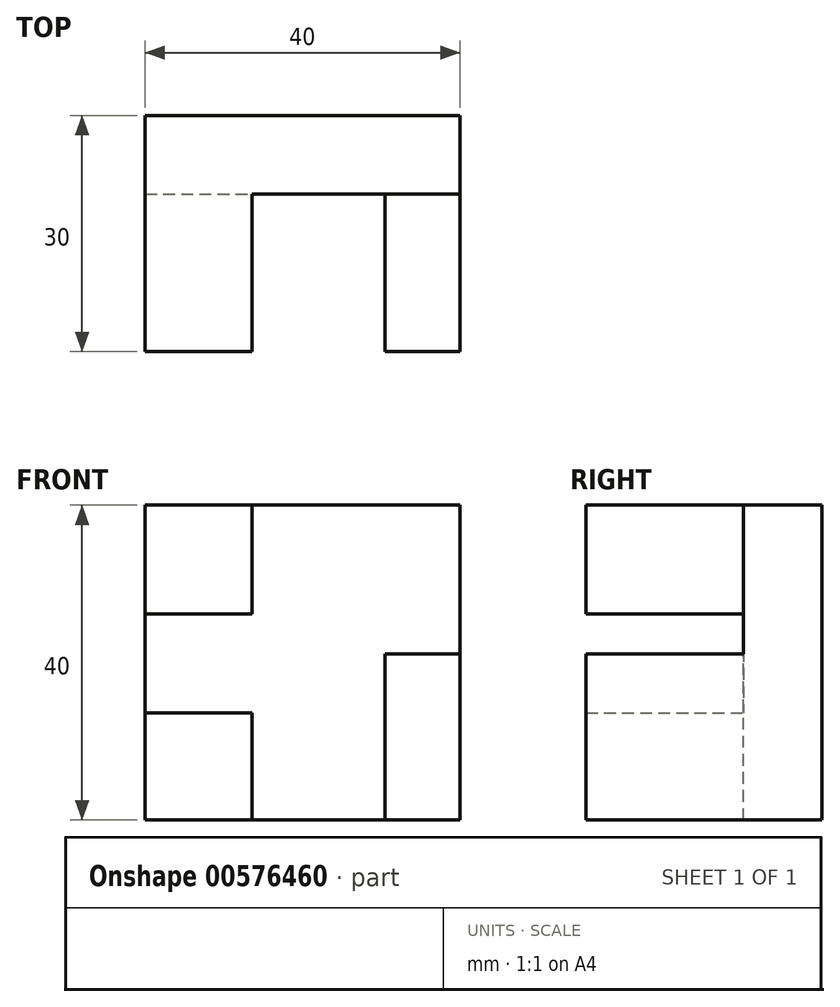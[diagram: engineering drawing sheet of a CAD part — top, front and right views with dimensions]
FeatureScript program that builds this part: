
annotation { "Feature Type Name" : "Feature", "Feature Type Description" : "" }
export const myFeature = defineFeature(function(context is Context, id is Id, definition is map)
    precondition{}
    {
        {
            var Q0;
            Q0=qCreatedBy(makeId("Front.planeOp"),FACE);
            var sketch = newSketch(context, id + "F0", { "sketchPlane" : qUnion([Q0])});
            skLineSegment(sketch, "E0.bottom", {"start": v(-28.84, 42.03) * mm, "end": v(11.16, 42.03) * mm});
            skLineSegment(sketch, "E0.top", {"start": v(-28.84, 2.03) * mm, "end": v(11.16, 2.03) * mm});
            skLineSegment(sketch, "E0.left", {"start": v(-28.84, 42.03) * mm, "end": v(-28.84, 2.03) * mm});
            skLineSegment(sketch, "E0.right", {"start": v(11.16, 42.03) * mm, "end": v(11.16, 2.03) * mm});
            skSolve(sketch);
        }
        {
            var Q0;
            Q0=makeQuery(id+"F0.imprint","IMPRINT",FACE,{"disambiguationData":[TD([[makeQuery(id+"F0.imprint","IMPRINT",EDGE,{"derivedFrom":sQuery(id+"F0.wireOp",EDGE,"E0.bottom")}),-1.0]])]});
            extrude(context, id + "F1", {"entities" : qUnion([Q0]), "depth" : 10 * mm, "offsetDistance" : 25 * mm});
        }
        {
            var Q0;
            Q0=makeQuery(id+"F1.opExtrude","CAP_FACE",FACE,{"disambiguationData":[OSD([sQuery(id+"F0.wireOp",EDGE,"E0.bottom"),sQuery(id+"F0.wireOp",EDGE,"E0.top"),sQuery(id+"F0.wireOp",EDGE,"E0.left"),sQuery(id+"F0.wireOp",EDGE,"E0.right")])],"isStart":false});
            var sketch = newSketch(context, id + "F2", { "sketchPlane" : qUnion([Q0])});
            skLineSegment(sketch, "E1.bottom", {"start": v(-28.84, 42.03) * mm, "end": v(-15.23, 42.03) * mm});
            skLineSegment(sketch, "E1.top", {"start": v(-28.84, 28.23) * mm, "end": v(-15.23, 28.23) * mm});
            skLineSegment(sketch, "E1.left", {"start": v(-28.84, 42.03) * mm, "end": v(-28.84, 28.23) * mm});
            skLineSegment(sketch, "E1.right", {"start": v(-15.23, 42.03) * mm, "end": v(-15.23, 28.23) * mm});
            skLineSegment(sketch, "E2.bottom", {"start": v(11.16, 2.03) * mm, "end": v(1.62, 2.03) * mm});
            skLineSegment(sketch, "E2.top", {"start": v(11.16, 23.15) * mm, "end": v(1.62, 23.15) * mm});
            skLineSegment(sketch, "E2.left", {"start": v(11.16, 2.03) * mm, "end": v(11.16, 23.15) * mm});
            skLineSegment(sketch, "E2.right", {"start": v(1.62, 2.03) * mm, "end": v(1.62, 23.15) * mm});
            skLineSegment(sketch, "E3.bottom", {"start": v(-15.23, 2.03) * mm, "end": v(-28.84, 2.03) * mm});
            skLineSegment(sketch, "E3.top", {"start": v(-15.23, 15.64) * mm, "end": v(-28.84, 15.64) * mm});
            skLineSegment(sketch, "E3.left", {"start": v(-15.23, 2.03) * mm, "end": v(-15.23, 15.64) * mm});
            skLineSegment(sketch, "E3.right", {"start": v(-28.84, 2.03) * mm, "end": v(-28.84, 15.64) * mm});
            skSolve(sketch);
        }
        {
            var Q0;
            Q0=makeQuery(id+"F2.imprint","IMPRINT",FACE,{"disambiguationData":[TD([[makeQuery(id+"F2.imprint","IMPRINT",EDGE,{"derivedFrom":sQuery(id+"F2.wireOp",EDGE,"E1.bottom")}),-1.0]])]});
            var Q1;
            Q1=makeQuery(id+"F2.imprint","IMPRINT",FACE,{"disambiguationData":[TD([[makeQuery(id+"F2.imprint","IMPRINT",EDGE,{"derivedFrom":sQuery(id+"F2.wireOp",EDGE,"E3.bottom")}),1.0]])]});
            var Q2;
            Q2=makeQuery(id+"F2.imprint","IMPRINT",FACE,{"disambiguationData":[TD([[makeQuery(id+"F2.imprint","IMPRINT",EDGE,{"derivedFrom":sQuery(id+"F2.wireOp",EDGE,"E2.bottom")}),1.0]])]});
            extrude(context, id + "F3", {"entities" : qUnion([Q0, Q1, Q2]), "operationType" : NewBodyOperationType.ADD, "depth" : 20 * mm, "offsetDistance" : 25 * mm});
        }
    });
